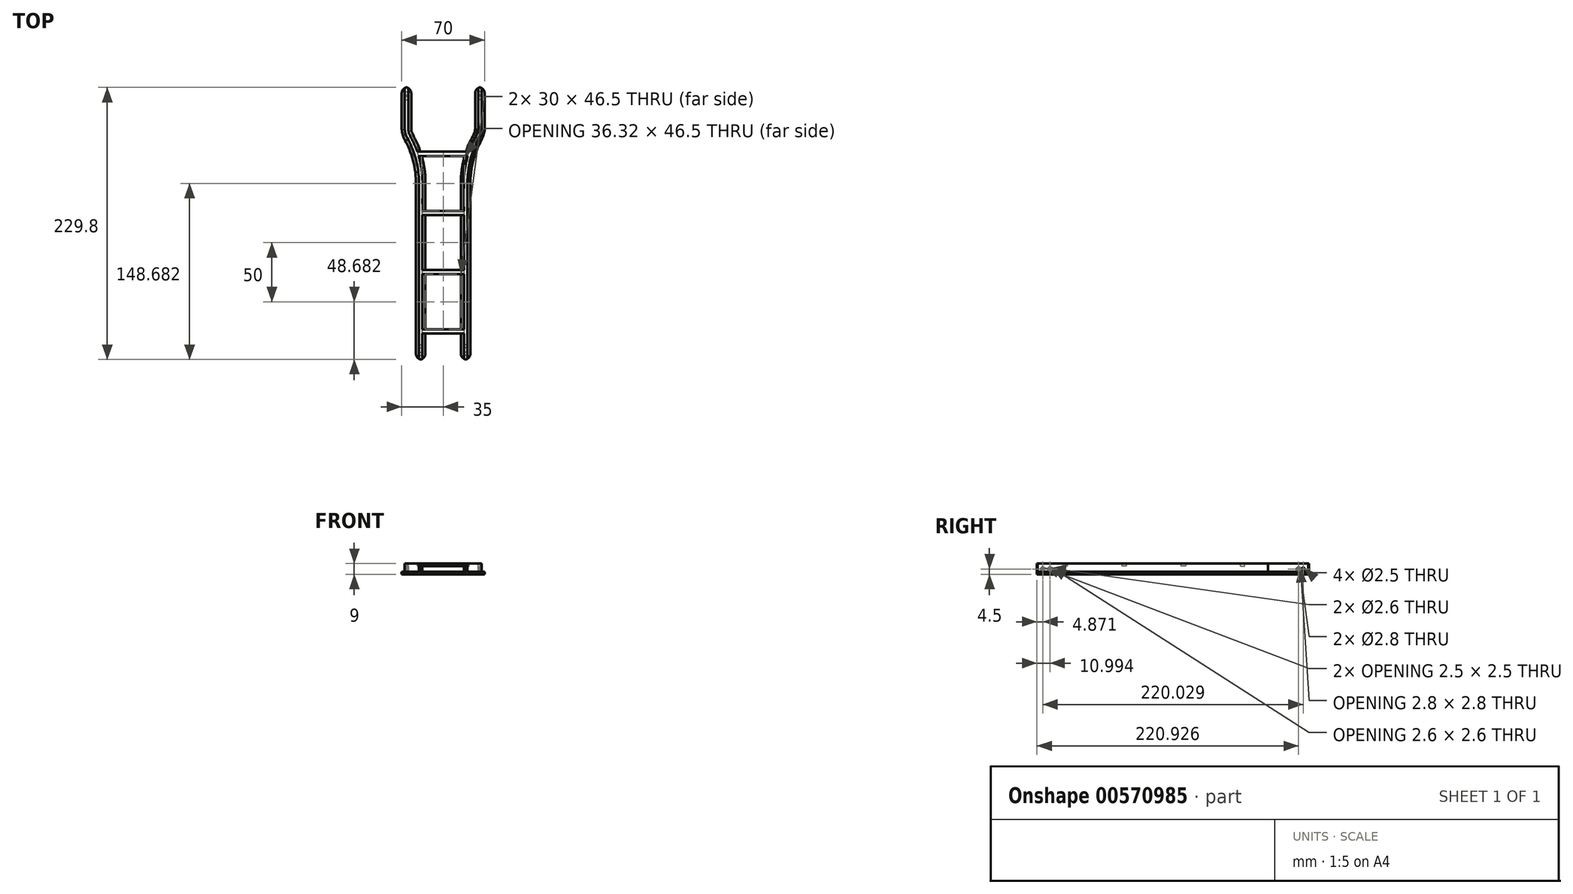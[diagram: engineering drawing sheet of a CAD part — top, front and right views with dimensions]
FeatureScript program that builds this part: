
annotation { "Feature Type Name" : "Feature", "Feature Type Description" : "" }
export const myFeature = defineFeature(function(context is Context, id is Id, definition is map)
    precondition{}
    {
        {
            var Q0;
            Q0=qCreatedBy(makeId("Front.planeOp"),FACE);
            var sketch = newSketch(context, id + "F0", { "sketchPlane" : qUnion([Q0])});
            skLineSegment(sketch, "E0.bottom", {"start": v(-15, 0) * mm, "end": v(-23, 0) * mm});
            skLineSegment(sketch, "E0.top", {"start": v(-15, 9) * mm, "end": v(-23, 9) * mm});
            skLineSegment(sketch, "E0.left", {"start": v(-15, 0) * mm, "end": v(-15, 2) * mm});
            skLineSegment(sketch, "E0.right", {"start": v(-23, 0) * mm, "end": v(-23, 2) * mm});
            skLineSegment(sketch, "E1.bottom", {"start": v(-23, 7) * mm, "end": v(-21, 7) * mm});
            skLineSegment(sketch, "E1.top", {"start": v(-23, 2) * mm, "end": v(-21, 2) * mm});
            skLineSegment(sketch, "E1.right", {"start": v(-20.5, 6.5) * mm, "end": v(-20.5, 2.5) * mm});
            skLineSegment(sketch, "E2.bottom", {"start": v(-17, 7) * mm, "end": v(-15, 7) * mm});
            skLineSegment(sketch, "E2.top", {"start": v(-17, 2) * mm, "end": v(-15, 2) * mm});
            skLineSegment(sketch, "E2.left", {"start": v(-17.5, 6.5) * mm, "end": v(-17.5, 2.5) * mm});
            skLineSegment(sketch, "E3", {"start": v(-19, 9) * mm, "end": v(-19, -4.59) * mm, "construction": true});
            skPoint(sketch, "E3.endSnap0", {"position": v(-19, 0) * mm});
            skLineSegment(sketch, "E4.trimOffspring", {"start": v(-15, 7) * mm, "end": v(-15, 9) * mm});
            skLineSegment(sketch, "E5.trimOffspring", {"start": v(-23, 7) * mm, "end": v(-23, 9) * mm});
            skPoint(sketch, "E6.visualSharp", {"position": v(-20.5, 7) * mm});
            skArc(sketch, "E6.filletArc", {"start": v(-20.5, 6.5) * mm, "mid": v(-20.65, 6.85) * mm, "end": v(-21, 7) * mm});
            skPoint(sketch, "E7.visualSharp", {"position": v(-17.5, 7) * mm});
            skArc(sketch, "E7.filletArc", {"start": v(-17, 7) * mm, "mid": v(-17.35, 6.85) * mm, "end": v(-17.5, 6.5) * mm});
            skPoint(sketch, "E8.visualSharp", {"position": v(-17.5, 2) * mm});
            skArc(sketch, "E8.filletArc", {"start": v(-17.5, 2.5) * mm, "mid": v(-17.35, 2.15) * mm, "end": v(-17, 2) * mm});
            skPoint(sketch, "E9.visualSharp", {"position": v(-20.5, 2) * mm});
            skArc(sketch, "E9.filletArc", {"start": v(-21, 2) * mm, "mid": v(-20.65, 2.15) * mm, "end": v(-20.5, 2.5) * mm});
            skSolve(sketch);
        }
        {
            var Q0;
            Q0=qCreatedBy(makeId("Top.planeOp"),FACE);
            var sketch = newSketch(context, id + "F1", { "sketchPlane" : qUnion([Q0])});
            skLineSegment(sketch, "E10", {"start": v(-35.26, 0) * mm, "end": v(-35.26, 150) * mm});
            skLineSegment(sketch, "E11", {"start": v(-47.26, 230) * mm, "end": v(-47.26, 195) * mm});
            skFitSpline(sketch, "E12", {"points": [v(-35.26, 150) * mm, v(-40.7, 174.86) * mm, v(-47.26, 195) * mm], "startDerivative": vector(-0.38, 53.31) * mm, "endDerivative": vector(-0.87, 58.08) * mm});
            skSolve(sketch);
        }
        {
            var Q0;
            Q0=qSketchRegion(id+"F0",true);
            var Q1;
            Q1=qConstructionFilter(qBodyType(qCreatedBy(id+"F1",EDGE),BodyType.WIRE),ConstructionObject.NO);
            sweep(context, id + "F2", {"profiles" : qUnion([Q0]), "path" : qUnion([Q1])});
        }
        {
            var Q0;
            Q0=qCreatedBy(makeId("Front.planeOp"),FACE);
            var sketch = newSketch(context, id + "F3", { "sketchPlane" : qUnion([Q0])});
            skLineSegment(sketch, "E13.bottom", {"start": v(-17.5, 6.31) * mm, "end": v(-14.7, 6.31) * mm});
            skLineSegment(sketch, "E13.top", {"start": v(-17.5, 10.3) * mm, "end": v(-14.7, 10.3) * mm});
            skLineSegment(sketch, "E13.left", {"start": v(-17.5, 6.31) * mm, "end": v(-17.5, 10.3) * mm});
            skLineSegment(sketch, "E13.right", {"start": v(-14.7, 6.31) * mm, "end": v(-14.7, 10.3) * mm});
            skLineSegment(sketch, "E14.bottom", {"start": v(-20.5, 6.31) * mm, "end": v(-23, 6.31) * mm});
            skLineSegment(sketch, "E14.top", {"start": v(-20.5, 10.3) * mm, "end": v(-23, 10.3) * mm});
            skLineSegment(sketch, "E14.left", {"start": v(-20.5, 6.31) * mm, "end": v(-20.5, 10.3) * mm});
            skLineSegment(sketch, "E14.right", {"start": v(-23, 6.31) * mm, "end": v(-23, 10.3) * mm});
            skSolve(sketch);
        }
        {
            var Q0;
            Q0=makeQuery(id+"F2.opSweep","SWEPT_FACE",FACE,{"disambiguationData":[OSD([sQuery(id+"F0.wireOp",EDGE,"E4.trimOffspring"),sQuery(id+"F1.wireOp",EDGE,"E10")])]});
            var sketch = newSketch(context, id + "F4", { "sketchPlane" : qUnion([Q0])});
            skLineSegment(sketch, "E15.bottom", {"start": v(22.03, 9) * mm, "end": v(25.53, 9) * mm});
            skLineSegment(sketch, "E15.top", {"start": v(22.03, 7) * mm, "end": v(25.53, 7) * mm});
            skLineSegment(sketch, "E15.left", {"start": v(22.03, 9) * mm, "end": v(22.03, 7) * mm});
            skLineSegment(sketch, "E15.right", {"start": v(25.53, 9) * mm, "end": v(25.53, 7) * mm});
            skLineSegment(sketch, "E16.0.1.0", {"start": v(22.03, 2) * mm, "end": v(22.03, 0) * mm});
            skLineSegment(sketch, "E16.0.1.1", {"start": v(22.03, 0) * mm, "end": v(25.53, 0) * mm});
            skLineSegment(sketch, "E16.0.1.2", {"start": v(22.03, 2) * mm, "end": v(25.53, 2) * mm});
            skLineSegment(sketch, "E16.0.1.3", {"start": v(25.53, 2) * mm, "end": v(25.53, 0) * mm});
            skLineSegment(sketch, "E16.1.0.0", {"start": v(72.03, 9) * mm, "end": v(72.03, 7) * mm});
            skLineSegment(sketch, "E16.1.0.1", {"start": v(72.03, 7) * mm, "end": v(75.53, 7) * mm});
            skLineSegment(sketch, "E16.1.0.2", {"start": v(72.03, 9) * mm, "end": v(75.53, 9) * mm});
            skLineSegment(sketch, "E16.1.0.3", {"start": v(75.53, 9) * mm, "end": v(75.53, 7) * mm});
            skLineSegment(sketch, "E16.1.1.0", {"start": v(72.03, 2) * mm, "end": v(72.03, 0) * mm});
            skLineSegment(sketch, "E16.1.1.1", {"start": v(72.03, 0) * mm, "end": v(75.53, 0) * mm});
            skLineSegment(sketch, "E16.1.1.2", {"start": v(72.03, 2) * mm, "end": v(75.53, 2) * mm});
            skLineSegment(sketch, "E16.1.1.3", {"start": v(75.53, 2) * mm, "end": v(75.53, 0) * mm});
            skLineSegment(sketch, "E16.2.0.0", {"start": v(122.03, 9) * mm, "end": v(122.03, 7) * mm});
            skLineSegment(sketch, "E16.2.0.1", {"start": v(122.03, 7) * mm, "end": v(125.53, 7) * mm});
            skLineSegment(sketch, "E16.2.0.2", {"start": v(122.03, 9) * mm, "end": v(125.53, 9) * mm});
            skLineSegment(sketch, "E16.2.0.3", {"start": v(125.53, 9) * mm, "end": v(125.53, 7) * mm});
            skLineSegment(sketch, "E16.2.1.0", {"start": v(122.03, 2) * mm, "end": v(122.03, 0) * mm});
            skLineSegment(sketch, "E16.2.1.1", {"start": v(122.03, 0) * mm, "end": v(125.53, 0) * mm});
            skLineSegment(sketch, "E16.2.1.2", {"start": v(122.03, 2) * mm, "end": v(125.53, 2) * mm});
            skLineSegment(sketch, "E16.2.1.3", {"start": v(125.53, 2) * mm, "end": v(125.53, 0) * mm});
            skLineSegment(sketch, "E16.3.0.0", {"start": v(172.03, 9) * mm, "end": v(172.03, 7) * mm});
            skLineSegment(sketch, "E16.3.0.1", {"start": v(172.03, 7) * mm, "end": v(175.53, 7) * mm});
            skLineSegment(sketch, "E16.3.0.2", {"start": v(172.03, 9) * mm, "end": v(175.53, 9) * mm});
            skLineSegment(sketch, "E16.3.0.3", {"start": v(175.53, 9) * mm, "end": v(175.53, 7) * mm});
            skLineSegment(sketch, "E16.3.1.0", {"start": v(172.03, 2) * mm, "end": v(172.03, 0) * mm});
            skLineSegment(sketch, "E16.3.1.1", {"start": v(172.03, 0) * mm, "end": v(175.53, 0) * mm});
            skLineSegment(sketch, "E16.3.1.2", {"start": v(172.03, 2) * mm, "end": v(175.53, 2) * mm});
            skLineSegment(sketch, "E16.3.1.3", {"start": v(175.53, 2) * mm, "end": v(175.53, 0) * mm});
            skLineSegment(sketch, "E16.direction1", {"start": v(22.03, 7) * mm, "end": v(72.03, 7) * mm, "construction": true});
            skLineSegment(sketch, "E16.direction2", {"start": v(22.03, 7) * mm, "end": v(22.03, 0) * mm, "construction": true});
            skSolve(sketch);
        }
        {
            var Q0;
            Q0=qSketchRegion(id+"F4",true);
            extrude(context, id + "F5", {"entities" : qUnion([Q0]), "operationType" : NewBodyOperationType.ADD, "depth" : 15 * mm});
        }
        {
            var Q0;
            Q0=makeQuery(id+"F5.opExtrude","CAP_FACE",FACE,{"disambiguationData":[OSD([sQuery(id+"F4.wireOp",EDGE,"E16.3.0.0"),sQuery(id+"F4.wireOp",EDGE,"E16.3.0.1"),sQuery(id+"F4.wireOp",EDGE,"E16.3.0.2"),sQuery(id+"F4.wireOp",EDGE,"E16.3.0.3")])],"isStart":true});
            var sketch = newSketch(context, id + "F6", { "sketchPlane" : qUnion([Q0])});
            skLineSegment(sketch, "E17.0", {"start": v(-172.03, 7) * mm, "end": v(-175.53, 7) * mm});
            skLineSegment(sketch, "E18.0.0", {"start": v(-175.53, 9) * mm, "end": v(-175.53, 7) * mm});
            skLineSegment(sketch, "E18.0.1", {"start": v(-175.53, 7) * mm, "end": v(-172.03, 7) * mm});
            skLineSegment(sketch, "E18.0.2", {"start": v(-172.03, 7) * mm, "end": v(-172.03, 9) * mm});
            skLineSegment(sketch, "E18.0.3", {"start": v(-172.03, 9) * mm, "end": v(-175.53, 9) * mm});
            skLineSegment(sketch, "E19.0.0", {"start": v(-175.53, 2) * mm, "end": v(-175.53, 0) * mm});
            skLineSegment(sketch, "E19.0.1", {"start": v(-175.53, 0) * mm, "end": v(-172.03, 0) * mm});
            skLineSegment(sketch, "E19.0.2", {"start": v(-172.03, 0) * mm, "end": v(-172.03, 2) * mm});
            skLineSegment(sketch, "E19.0.3", {"start": v(-172.03, 2) * mm, "end": v(-175.53, 2) * mm});
            skSolve(sketch);
        }
        {
            var Q0;
            Q0=qSketchRegion(id+"F6",true);
            extrude(context, id + "F7", {"entities" : qUnion([Q0]), "operationType" : NewBodyOperationType.ADD, "endBound" : BoundingType.UP_TO_NEXT, "depth" : 25 * mm});
        }
        {
            var Q0;
            Q0=qSketchRegion(id+"F3",true);
            var Q1;
            Q1=qConstructionFilter(qBodyType(qCreatedBy(id+"F1",EDGE),BodyType.WIRE),ConstructionObject.NO);
            sweep(context, id + "F8", {"operationType" : NewBodyOperationType.REMOVE, "profiles" : qUnion([Q0]), "path" : qUnion([Q1])});
        }
        {
            var Q0;
            Q0=qCreatedBy(makeId("Right.planeOp"),FACE);
            var sketch = newSketch(context, id + "F9", { "sketchPlane" : qUnion([Q0])});
            skLineSegment(sketch, "E20.0.0", {"start": v(25.53, 7) * mm, "end": v(25.53, 9) * mm});
            skLineSegment(sketch, "E20.0.1", {"start": v(25.53, 9) * mm, "end": v(22.03, 9) * mm});
            skLineSegment(sketch, "E20.0.2", {"start": v(22.03, 9) * mm, "end": v(22.03, 7) * mm});
            skLineSegment(sketch, "E20.0.3", {"start": v(22.03, 7) * mm, "end": v(25.53, 7) * mm});
            skLineSegment(sketch, "E21.0.0", {"start": v(75.53, 7) * mm, "end": v(75.53, 9) * mm});
            skLineSegment(sketch, "E21.0.1", {"start": v(75.53, 9) * mm, "end": v(72.03, 9) * mm});
            skLineSegment(sketch, "E21.0.2", {"start": v(72.03, 9) * mm, "end": v(72.03, 7) * mm});
            skLineSegment(sketch, "E21.0.3", {"start": v(72.03, 7) * mm, "end": v(75.53, 7) * mm});
            skLineSegment(sketch, "E22.0.0", {"start": v(175.53, 7) * mm, "end": v(175.53, 9) * mm});
            skLineSegment(sketch, "E22.0.1", {"start": v(175.53, 9) * mm, "end": v(172.03, 9) * mm});
            skLineSegment(sketch, "E22.0.2", {"start": v(172.03, 9) * mm, "end": v(172.03, 7) * mm});
            skLineSegment(sketch, "E22.0.3", {"start": v(172.03, 7) * mm, "end": v(175.53, 7) * mm});
            skLineSegment(sketch, "E23.0.0", {"start": v(125.53, 7) * mm, "end": v(125.53, 9) * mm});
            skLineSegment(sketch, "E23.0.1", {"start": v(125.53, 9) * mm, "end": v(122.03, 9) * mm});
            skLineSegment(sketch, "E23.0.2", {"start": v(122.03, 9) * mm, "end": v(122.03, 7) * mm});
            skLineSegment(sketch, "E23.0.3", {"start": v(122.03, 7) * mm, "end": v(125.53, 7) * mm});
            skSolve(sketch);
        }
        {
            var Q0;
            Q0=qSketchRegion(id+"F9",true);
            var Q1;
            Q1=makeQuery(id+"F8.boolean.opBoolean","SPLIT",BODY,{"disambiguationData":[OD(0.0)],"derivedFrom":makeQuery(id+"F2.opSweep","SWEPT_BODY",BODY,{"disambiguationData":[OSD([sQuery(id+"F0.wireOp",EDGE,"E0.bottom"),sQuery(id+"F0.wireOp",EDGE,"E0.top"),sQuery(id+"F0.wireOp",EDGE,"E0.left"),sQuery(id+"F0.wireOp",EDGE,"E0.right"),sQuery(id+"F0.wireOp",EDGE,"E1.bottom"),sQuery(id+"F0.wireOp",EDGE,"E1.top"),sQuery(id+"F0.wireOp",EDGE,"E1.right"),sQuery(id+"F0.wireOp",EDGE,"E2.bottom"),sQuery(id+"F0.wireOp",EDGE,"E2.top"),sQuery(id+"F0.wireOp",EDGE,"E2.left"),sQuery(id+"F0.wireOp",EDGE,"E4.trimOffspring"),sQuery(id+"F0.wireOp",EDGE,"E5.trimOffspring"),sQuery(id+"F0.wireOp",EDGE,"E6.filletArc"),sQuery(id+"F0.wireOp",EDGE,"E7.filletArc"),sQuery(id+"F0.wireOp",EDGE,"E8.filletArc"),sQuery(id+"F0.wireOp",EDGE,"E9.filletArc"),sQuery(id+"F1.wireOp",EDGE,"E11")])]})});
            extrude(context, id + "F10", {"entities" : qUnion([Q0]), "operationType" : NewBodyOperationType.ADD, "endBound" : BoundingType.UP_TO_BODY, "oppositeDirection" : true, "depth" : 25 * mm, "endBoundEntityBody" : qUnion([Q1]), "offsetDistance" : 25 * mm});
        }
        {
            var Q0;
            {var subQ0=sQuery(id+"F1.wireOp",EDGE,"E10");Q0=makeQuery(id+"F8.boolean.opBoolean","MERGE",FACE,{"derivedFrom":[makeQuery(id+"F2.opSweep","SWEPT_FACE",FACE,{"disambiguationData":[OSD([sQuery(id+"F0.wireOp",EDGE,"E2.left"),subQ0])]}),makeQuery(id+"F8.opSweep","SWEPT_FACE",FACE,{"disambiguationData":[OSD([subQ0,sQuery(id+"F3.wireOp",EDGE,"E13.left")])]})]});}
            var sketch = newSketch(context, id + "F11", { "sketchPlane" : qUnion([Q0])});
            skCircle(sketch, "E24", {"center": v(4.97, 4.5) * mm, "radius": 1.25 * mm});
            skCircle(sketch, "E25", {"center": v(11.1, 4.5) * mm, "radius": 1.3 * mm});
            skCircle(sketch, "E26", {"center": v(225, 4.5) * mm, "radius": 1.25 * mm});
            skCircle(sketch, "E27", {"center": v(221.03, 4.5) * mm, "radius": 1.4 * mm});
            skSolve(sketch);
        }
        {
            var Q0;
            Q0=qSketchRegion(id+"F11",true);
            extrude(context, id + "F12", {"entities" : qUnion([Q0]), "operationType" : NewBodyOperationType.REMOVE, "endBound" : BoundingType.THROUGH_ALL, "oppositeDirection" : true, "depth" : 25 * mm, "offsetDistance" : 25 * mm});
        }
        {
            var Q0;
            Q0=makeQuery(id+"F2.opSweep","CAP_EDGE",EDGE,{"disambiguationData":[OSD([sQuery(id+"F0.wireOp",EDGE,"E0.left"),sQuery(id+"F1.wireOp",VERTEX,"E10.start")])],"isStart":true});
            var Q1;
            Q1=makeQuery(id+"F2.opSweep","CAP_EDGE",EDGE,{"disambiguationData":[OSD([sQuery(id+"F0.wireOp",EDGE,"E0.right"),sQuery(id+"F1.wireOp",VERTEX,"E10.start")])],"isStart":true});
            var Q2;
            Q2=makeQuery(id+"F2.opSweep","CAP_EDGE",EDGE,{"disambiguationData":[OSD([sQuery(id+"F0.wireOp",EDGE,"E0.right"),sQuery(id+"F1.wireOp",VERTEX,"E11.start")])],"isStart":false});
            var Q3;
            Q3=makeQuery(id+"F2.opSweep","CAP_EDGE",EDGE,{"disambiguationData":[OSD([sQuery(id+"F0.wireOp",EDGE,"E0.left"),sQuery(id+"F1.wireOp",VERTEX,"E11.start")])],"isStart":false});
            fillet(context, id + "F13", {"entities" : qUnion([Q0, Q1, Q2, Q3]), "radius" : 5 * mm, "tangentPropagation" : true, "allowEdgeOverflow" : false});
        }
        {
            var Q0;
            Q0=makeQuery(id+"F8.boolean.opBoolean","SPLIT",BODY,{"disambiguationData":[OD(0.0)],"derivedFrom":makeQuery(id+"F2.opSweep","SWEPT_BODY",BODY,{"disambiguationData":[OSD([sQuery(id+"F0.wireOp",EDGE,"E0.bottom"),sQuery(id+"F0.wireOp",EDGE,"E0.top"),sQuery(id+"F0.wireOp",EDGE,"E0.left"),sQuery(id+"F0.wireOp",EDGE,"E0.right"),sQuery(id+"F0.wireOp",EDGE,"E1.bottom"),sQuery(id+"F0.wireOp",EDGE,"E1.top"),sQuery(id+"F0.wireOp",EDGE,"E1.right"),sQuery(id+"F0.wireOp",EDGE,"E2.bottom"),sQuery(id+"F0.wireOp",EDGE,"E2.top"),sQuery(id+"F0.wireOp",EDGE,"E2.left"),sQuery(id+"F0.wireOp",EDGE,"E4.trimOffspring"),sQuery(id+"F0.wireOp",EDGE,"E5.trimOffspring"),sQuery(id+"F0.wireOp",EDGE,"E6.filletArc"),sQuery(id+"F0.wireOp",EDGE,"E7.filletArc"),sQuery(id+"F0.wireOp",EDGE,"E8.filletArc"),sQuery(id+"F0.wireOp",EDGE,"E9.filletArc"),sQuery(id+"F1.wireOp",EDGE,"E11")])]})});
            var Q1;
            Q1=makeQuery(id+"F5.opExtrude","CAP_FACE",FACE,{"disambiguationData":[OSD([sQuery(id+"F4.wireOp",EDGE,"E15.bottom"),sQuery(id+"F4.wireOp",EDGE,"E15.top"),sQuery(id+"F4.wireOp",EDGE,"E15.left"),sQuery(id+"F4.wireOp",EDGE,"E15.right")])],"isStart":false});
            mirror(context, id + "F14", {"operationType" : NewBodyOperationType.ADD, "entities" : qUnion([Q0]), "mirrorPlane" : qUnion([Q1])});
        }
    });
